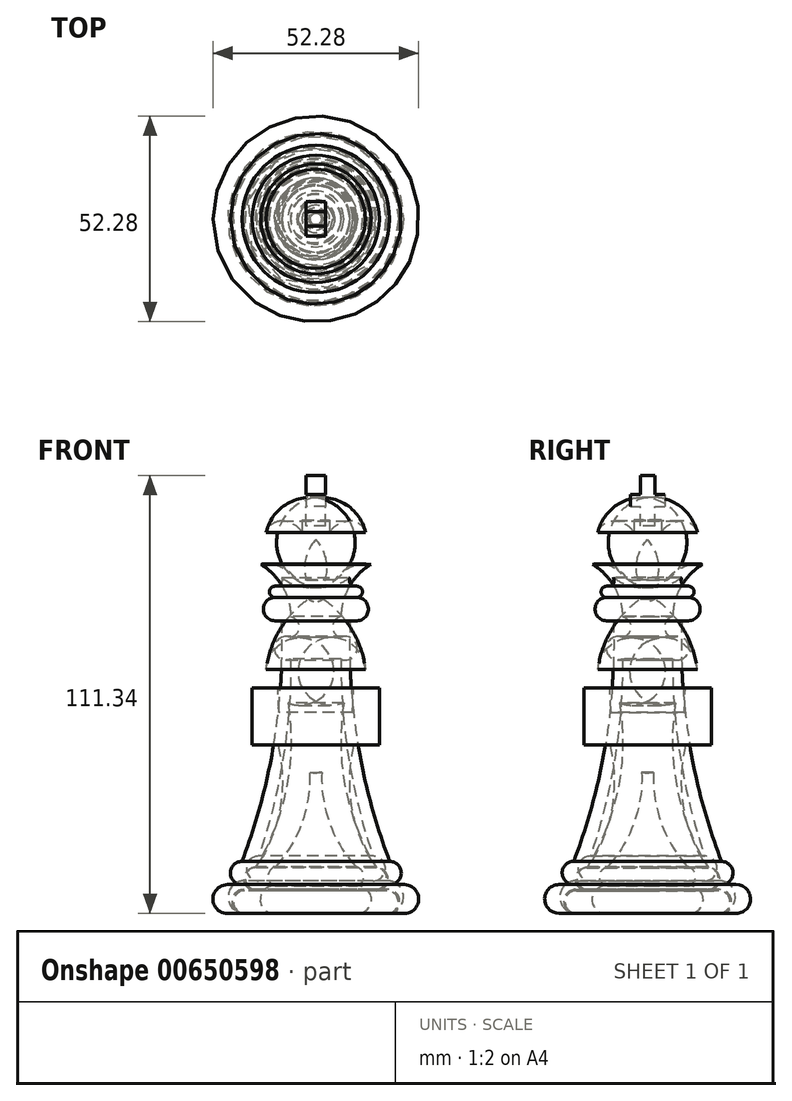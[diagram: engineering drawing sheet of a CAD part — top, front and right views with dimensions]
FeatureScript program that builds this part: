
annotation { "Feature Type Name" : "Feature", "Feature Type Description" : "" }
export const myFeature = defineFeature(function(context is Context, id is Id, definition is map)
    precondition{}
    {
        {
            var Q0;
            Q0=qCreatedBy(makeId("Front.planeOp"),FACE);
            var sketch = newSketch(context, id + "F0", { "sketchPlane" : qUnion([Q0])});
            skArc(sketch, "E0", {"start": v(0, 45.94) * mm, "mid": v(-5.38, 41.6) * mm, "end": v(-1.5, 35.88) * mm});
            skArc(sketch, "E1", {"start": v(-10.14, 11.85) * mm, "mid": v(-3.46, 23.01) * mm, "end": v(-1.5, 35.88) * mm});
            skLineSegment(sketch, "E2", {"start": v(-10.14, 0) * mm, "end": v(0, 0) * mm});
            skLineSegment(sketch, "E3", {"start": v(0, 0) * mm, "end": v(0, 45.94) * mm});
            skArc(sketch, "E4", {"start": v(-10.14, 6.93) * mm, "mid": v(-14.13, 3.46) * mm, "end": v(-10.14, 0) * mm});
            skArc(sketch, "E5", {"start": v(-10.14, 11.85) * mm, "mid": v(-12.16, 9.39) * mm, "end": v(-10.14, 6.93) * mm});
            skSolve(sketch);
        }
        {
            var Q0;
            Q0=makeQuery(id+"F0.imprint","IMPRINT",FACE,{"disambiguationData":[TD([[makeQuery(id+"F0.imprint","IMPRINT",EDGE,{"derivedFrom":sQuery(id+"F0.wireOp",EDGE,"E0")}),1.0]])]});
            var Q1;
            Q1=sQuery(id+"F0.wireOp",EDGE,"E3");
            revolve(context, id + "F1", {"entities" : qUnion([Q0]), "axis" : qUnion([Q1]), "revolveType" : RevolveType.FULL});
        }
        {
            var Q0;
            Q0=qCreatedBy(makeId("Front.planeOp"),FACE);
            var sketch = newSketch(context, id + "F2", { "sketchPlane" : qUnion([Q0])});
            skLineSegment(sketch, "E6", {"start": v(0, 0) * mm, "end": v(0, 84.7) * mm, "construction": true});
            skLineSegment(sketch, "E7", {"start": v(0, 0) * mm, "end": v(-18.13, 0) * mm});
            skArc(sketch, "E8", {"start": v(-18.13, 8.29) * mm, "mid": v(-22.27, 4.14) * mm, "end": v(-18.13, 0) * mm});
            skLineSegment(sketch, "E9", {"start": v(-18.13, 8.29) * mm, "end": v(-14.53, 8.29) * mm});
            skArc(sketch, "E10", {"start": v(-14.53, 14.55) * mm, "mid": v(-17.66, 11.42) * mm, "end": v(-14.53, 8.29) * mm});
            skArc(sketch, "E11", {"start": v(-14.53, 14.55) * mm, "mid": v(-8.36, 39.23) * mm, "end": v(-6.37, 64.6) * mm});
            skArc(sketch, "E12", {"start": v(-6.37, 70.1) * mm, "mid": v(-10.53, 67.35) * mm, "end": v(-6.37, 64.6) * mm});
            skArc(sketch, "E13", {"start": v(-6.37, 70.1) * mm, "mid": v(-4.28, 72.75) * mm, "end": v(-6.37, 75.4) * mm});
            skArc(sketch, "E14", {"start": v(-6.37, 75.4) * mm, "mid": v(-8.47, 83.01) * mm, "end": v(-13.96, 88.68) * mm});
            skArc(sketch, "E15", {"start": v(-4.86, 84.7) * mm, "mid": v(-8.86, 87.95) * mm, "end": v(-13.96, 88.68) * mm});
            skLineSegment(sketch, "E16", {"start": v(-4.86, 84.7) * mm, "end": v(-2.4, 84.7) * mm});
            skArc(sketch, "E17", {"start": v(0, 94.93) * mm, "mid": v(-2.58, 90.14) * mm, "end": v(-2.4, 84.7) * mm});
            skLineSegment(sketch, "E18", {"start": v(0, 94.93) * mm, "end": v(0, 0) * mm});
            skSolve(sketch);
        }
        {
            var Q0;
            Q0=makeQuery(id+"F2.imprint","IMPRINT",FACE,{"disambiguationData":[TD([[makeQuery(id+"F2.imprint","IMPRINT",EDGE,{"derivedFrom":sQuery(id+"F2.wireOp",EDGE,"E7")}),-1.0]])]});
            var Q1;
            Q1=sQuery(id+"F2.wireOp",EDGE,"E18");
            revolve(context, id + "F3", {"entities" : qUnion([Q0]), "axis" : qUnion([Q1]), "revolveType" : RevolveType.FULL});
        }
        {
            var Q0;
            Q0=qCreatedBy(makeId("Front.planeOp"),FACE);
            var sketch = newSketch(context, id + "F4", { "sketchPlane" : qUnion([Q0])});
            skLineSegment(sketch, "E19", {"start": v(0, 0) * mm, "end": v(-18.29, 0) * mm});
            skArc(sketch, "E20", {"start": v(-18.29, 6.06) * mm, "mid": v(-21.32, 3.03) * mm, "end": v(-18.29, 0) * mm});
            skLineSegment(sketch, "E21", {"start": v(-18.29, 6.06) * mm, "end": v(-15.12, 6.06) * mm});
            skArc(sketch, "E22", {"start": v(-15.12, 11.76) * mm, "mid": v(-17.97, 8.91) * mm, "end": v(-15.12, 6.06) * mm});
            skArc(sketch, "E23", {"start": v(-15.12, 11.76) * mm, "mid": v(-9.1, 26.73) * mm, "end": v(-9.62, 42.84) * mm});
            skLineSegment(sketch, "E24", {"start": v(-9.62, 42.84) * mm, "end": v(-16.17, 42.84) * mm});
            skLineSegment(sketch, "E25", {"start": v(-16.17, 42.84) * mm, "end": v(-16.17, 57.22) * mm});
            skLineSegment(sketch, "E26", {"start": v(-9.62, 57.22) * mm, "end": v(-16.17, 57.22) * mm});
            skLineSegment(sketch, "E27", {"start": v(-9.62, 57.22) * mm, "end": v(-9.32, 51.07) * mm});
            skLineSegment(sketch, "E28", {"start": v(-9.32, 51.07) * mm, "end": v(0, 51.07) * mm});
            skLineSegment(sketch, "E29", {"start": v(0, 51.07) * mm, "end": v(0, 0) * mm});
            skSolve(sketch);
        }
        {
            var Q0;
            Q0=makeQuery(id+"F4.imprint","IMPRINT",FACE,{"disambiguationData":[TD([[makeQuery(id+"F4.imprint","IMPRINT",EDGE,{"derivedFrom":sQuery(id+"F4.wireOp",EDGE,"E19")}),-1.0]])]});
            var Q1;
            Q1=sQuery(id+"F4.wireOp",EDGE,"E29");
            revolve(context, id + "F5", {"entities" : qUnion([Q0]), "axis" : qUnion([Q1]), "revolveType" : RevolveType.FULL});
        }
        {
            var Q0;
            Q0=qCreatedBy(makeId("Right.planeOp"),FACE);
            var sketch = newSketch(context, id + "F6", { "sketchPlane" : qUnion([Q0])});
            skLineSegment(sketch, "E30", {"start": v(0, 0) * mm, "end": v(-18.08, 0) * mm});
            skArc(sketch, "E31", {"start": v(-18.08, 5.78) * mm, "mid": v(-20.97, 2.89) * mm, "end": v(-18.08, 0) * mm});
            skLineSegment(sketch, "E32", {"start": v(-18.08, 5.78) * mm, "end": v(-15.42, 5.78) * mm});
            skLineSegment(sketch, "E33", {"start": v(0, 73.2) * mm, "end": v(0, 0) * mm});
            skArc(sketch, "E34", {"start": v(-15.42, 11.6) * mm, "mid": v(-18.33, 8.68) * mm, "end": v(-15.42, 5.78) * mm});
            skLineSegment(sketch, "E35", {"start": v(0, 73.2) * mm, "end": v(0, 83.46) * mm});
            skArc(sketch, "E36", {"start": v(-1.83, 79.93) * mm, "mid": v(-9.12, 72.13) * mm, "end": v(-12.6, 62.03) * mm});
            skArc(sketch, "E37", {"start": v(0, 83.46) * mm, "mid": v(-2.17, 82.34) * mm, "end": v(-1.83, 79.93) * mm});
            skArc(sketch, "E38", {"start": v(-12.6, 62.03) * mm, "mid": v(-11.26, 56.84) * mm, "end": v(-7.1, 53.45) * mm});
            skArc(sketch, "E39", {"start": v(-15.42, 11.6) * mm, "mid": v(-7.52, 31.78) * mm, "end": v(-7.1, 53.45) * mm});
            skSolve(sketch);
        }
        {
            var Q0;
            Q0=makeQuery(id+"F6.imprint","IMPRINT",FACE,{"disambiguationData":[TD([[makeQuery(id+"F6.imprint","IMPRINT",EDGE,{"derivedFrom":sQuery(id+"F6.wireOp",EDGE,"E30")}),-1.0]])]});
            var Q1;
            Q1=sQuery(id+"F6.wireOp",EDGE,"E33");
            revolve(context, id + "F7", {"entities" : qUnion([Q0]), "axis" : qUnion([Q1]), "revolveType" : RevolveType.FULL});
        }
        {
            var Q0;
            Q0=qCreatedBy(makeId("Right.planeOp"),FACE);
            var sketch = newSketch(context, id + "F8", { "sketchPlane" : qUnion([Q0])});
            skLineSegment(sketch, "E40", {"start": v(0, 0) * mm, "end": v(-22.5, 0) * mm});
            skArc(sketch, "E41", {"start": v(-22.5, 7.3) * mm, "mid": v(-26.14, 3.65) * mm, "end": v(-22.5, 0) * mm});
            skLineSegment(sketch, "E42", {"start": v(-22.5, 7.3) * mm, "end": v(-18.74, 7.3) * mm});
            skArc(sketch, "E43", {"start": v(-18.74, 13.22) * mm, "mid": v(-21.7, 10.26) * mm, "end": v(-18.74, 7.3) * mm});
            skLineSegment(sketch, "E44", {"start": v(0, 0) * mm, "end": v(0, 99.96) * mm, "construction": true});
            skArc(sketch, "E45", {"start": v(-18.74, 13.22) * mm, "mid": v(-10.65, 43.28) * mm, "end": v(-8.72, 74.35) * mm});
            skLineSegment(sketch, "E46", {"start": v(-8.72, 74.35) * mm, "end": v(-10.4, 74.35) * mm});
            skArc(sketch, "E47", {"start": v(-10.4, 80.27) * mm, "mid": v(-13.35, 77.31) * mm, "end": v(-10.4, 74.35) * mm});
            skArc(sketch, "E48", {"start": v(-10.4, 83.13) * mm, "mid": v(-11.83, 81.7) * mm, "end": v(-10.4, 80.27) * mm});
            skArc(sketch, "E49", {"start": v(-10.4, 83.13) * mm, "mid": v(-8.8, 83.7) * mm, "end": v(-8.72, 85.4) * mm});
            skArc(sketch, "E50", {"start": v(-12.61, 96.83) * mm, "mid": v(-12.3, 90.56) * mm, "end": v(-8.72, 85.4) * mm});
            skArc(sketch, "E51", {"start": v(-8.72, 99.7) * mm, "mid": v(-11.13, 98.89) * mm, "end": v(-12.61, 96.83) * mm});
            skArc(sketch, "E52", {"start": v(-3.5, 96.83) * mm, "mid": v(-5.74, 98.93) * mm, "end": v(-8.72, 99.7) * mm});
            skLineSegment(sketch, "E53", {"start": v(-3.5, 96.83) * mm, "end": v(-3.5, 99.9) * mm});
            skLineSegment(sketch, "E54", {"start": v(-3.5, 99.9) * mm, "end": v(0, 99.9) * mm});
            skLineSegment(sketch, "E55", {"start": v(0, 0) * mm, "end": v(0, 99.9) * mm});
            skSolve(sketch);
        }
        {
            var Q0;
            Q0 = qSketchRegion(id + "F8", true);
            var Q1;
            Q1=sQuery(id+"F8.wireOp",EDGE,"E44");
            revolve(context, id + "F9", {"entities" : qUnion([Q0]), "axis" : qUnion([Q1]), "revolveType" : RevolveType.FULL});
        }
        {
            var Q0;
            Q0=qCreatedBy(makeId("Right.planeOp"),FACE);
            var sketch = newSketch(context, id + "F10", { "sketchPlane" : qUnion([Q0])});
            skLineSegment(sketch, "E56.bottom", {"start": v(1.8, 98.42) * mm, "end": v(-1.8, 98.42) * mm});
            skLineSegment(sketch, "E56.top", {"start": v(1.8, 111.31) * mm, "end": v(-1.8, 111.31) * mm});
            skLineSegment(sketch, "E56.left", {"start": v(1.8, 98.42) * mm, "end": v(1.8, 111.31) * mm});
            skLineSegment(sketch, "E56.right", {"start": v(-1.8, 98.42) * mm, "end": v(-1.8, 111.31) * mm});
            skPoint(sketch, "E56.middle", {"position": v(0, 104.87) * mm});
            skLineSegment(sketch, "E57.bottom", {"start": v(-4.4, 106.38) * mm, "end": v(4.4, 106.38) * mm});
            skLineSegment(sketch, "E57.top", {"start": v(-4.4, 103.35) * mm, "end": v(4.4, 103.35) * mm});
            skLineSegment(sketch, "E57.left", {"start": v(-4.4, 106.38) * mm, "end": v(-4.4, 103.35) * mm});
            skLineSegment(sketch, "E57.right", {"start": v(4.4, 106.38) * mm, "end": v(4.4, 103.35) * mm});
            skSolve(sketch);
        }
        {
            var Q0;
            {var subQ5=sQuery(id+"F10.wireOp",EDGE,"E57.left");Q0=makeQuery(id+"F10.imprint","IMPRINT",FACE,{"disambiguationData":[TD([[makeQuery(id+"F10.imprint","IMPRINT",EDGE,{"derivedFrom":subQ5}),1.0]])]});}
            var Q1;
            {var subQ0=sQuery(id+"F10.wireOp",EDGE,"E57.top");var subQ1=sQuery(id+"F10.wireOp",EDGE,"E56.left");var subQ2=makeQuery(id+"F10.imprint","INTERSECT",VERTEX,{"derivedFrom":[subQ1,subQ0]});Q1=makeQuery(id+"F10.imprint","IMPRINT",FACE,{"disambiguationData":[TD([[makeQuery(id+"F10.imprint","IMPRINT",EDGE,{"disambiguationData":[TD([[subQ2,-1.0]])],"derivedFrom":subQ1}),1.0]])]});}
            var Q2;
            {var subQ0=sQuery(id+"F10.wireOp",EDGE,"E56.bottom");Q2=makeQuery(id+"F10.imprint","IMPRINT",FACE,{"disambiguationData":[TD([[makeQuery(id+"F10.imprint","IMPRINT",EDGE,{"derivedFrom":subQ0}),-1.0]])]});}
            var Q3;
            {var subQ5=sQuery(id+"F10.wireOp",EDGE,"E57.right");Q3=makeQuery(id+"F10.imprint","IMPRINT",FACE,{"disambiguationData":[TD([[makeQuery(id+"F10.imprint","IMPRINT",EDGE,{"derivedFrom":subQ5}),-1.0]])]});}
            var Q4;
            {var subQ0=sQuery(id+"F10.wireOp",EDGE,"E56.top");Q4=makeQuery(id+"F10.imprint","IMPRINT",FACE,{"disambiguationData":[TD([[makeQuery(id+"F10.imprint","IMPRINT",EDGE,{"derivedFrom":subQ0}),1.0]])]});}
            extrude(context, id + "F11", {"entities" : qUnion([Q0, Q1, Q2, Q3, Q4]), "depth" : 5 * mm, "offsetDistance" : 25 * mm});
        }
        {
            var Q0;
            Q0=makeQuery(id+"F11.opExtrude","SWEPT_BODY",BODY,{"disambiguationData":[OSD([sQuery(id+"F10.wireOp",EDGE,"E56.bottom"),sQuery(id+"F10.wireOp",EDGE,"E56.top"),sQuery(id+"F10.wireOp",EDGE,"E56.left"),sQuery(id+"F10.wireOp",EDGE,"E56.right"),sQuery(id+"F10.wireOp",EDGE,"E57.bottom"),sQuery(id+"F10.wireOp",EDGE,"E57.top"),sQuery(id+"F10.wireOp",EDGE,"E57.left"),sQuery(id+"F10.wireOp",EDGE,"E57.right")])]});
            transform(context, id + "F12", {"entities" : qUnion([Q0]), "transformType" : TransformType.TRANSLATION_3D, "dx" : -2.5 * mm, "dy" : 0 * mm, "dz" : 0 * mm, "makeCopy" : false});
        }
    });
